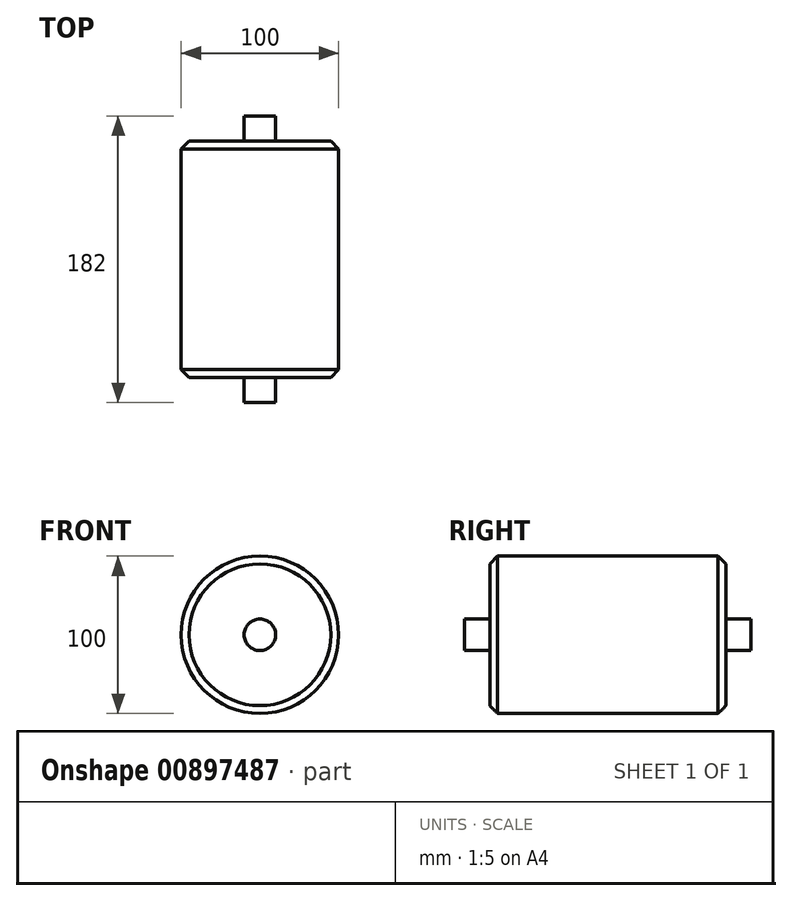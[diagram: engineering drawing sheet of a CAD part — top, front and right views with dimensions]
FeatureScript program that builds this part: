
annotation { "Feature Type Name" : "Feature", "Feature Type Description" : "" }
export const myFeature = defineFeature(function(context is Context, id is Id, definition is map)
    precondition{}
    {
        {
            var Q0;
            Q0=qCreatedBy(makeId("Front.planeOp"),FACE);
            var sketch = newSketch(context, id + "F0", { "sketchPlane" : qUnion([Q0])});
            skCircle(sketch, "E0", {"center": v(0, 0) * mm, "radius": 50 * mm});
            skSolve(sketch);
        }
        {
            var Q0;
            Q0 = qSketchRegion(id + "F0", true);
            extrude(context, id + "F1", {"entities" : qUnion([Q0]), "depth" : 75 * mm, "offsetDistance" : 25.4 * mm, "hasSecondDirection" : true, "secondDirectionOppositeDirection" : true, "secondDirectionDepth" : 75 * mm});
        }
        {
            var Q0;
            Q0=makeQuery(id+"F1.opExtrude","CAP_FACE",FACE,{"disambiguationData":[OSD([sQuery(id+"F0.wireOp",EDGE,"E0")])],"isStart":true});
            var sketch = newSketch(context, id + "F2", { "sketchPlane" : qUnion([Q0])});
            skCircle(sketch, "E1", {"center": v(0, 0) * mm, "radius": 10 * mm});
            skSolve(sketch);
        }
        {
            var Q0;
            Q0 = qSketchRegion(id + "F2", true);
            extrude(context, id + "F3", {"entities" : qUnion([Q0]), "operationType" : NewBodyOperationType.ADD, "depth" : 16 * mm, "offsetDistance" : 25.4 * mm});
        }
        {
            var Q0;
            Q0=makeQuery(id+"F1.opExtrude","CAP_FACE",FACE,{"disambiguationData":[OSD([sQuery(id+"F0.wireOp",EDGE,"E0")])],"isStart":false});
            var sketch = newSketch(context, id + "F4", { "sketchPlane" : qUnion([Q0])});
            skCircle(sketch, "E2", {"center": v(0, 0) * mm, "radius": 10 * mm});
            skSolve(sketch);
        }
        {
            var Q0;
            Q0 = qSketchRegion(id + "F4", true);
            extrude(context, id + "F5", {"entities" : qUnion([Q0]), "operationType" : NewBodyOperationType.ADD, "depth" : 16 * mm, "offsetDistance" : 25.4 * mm});
        }
        {
            var Q0;
            Q0=makeQuery(id+"F1.opExtrude","CAP_EDGE",EDGE,{"disambiguationData":[OSD([sQuery(id+"F0.wireOp",EDGE,"E0")])],"isStart":false});
            chamfer(context, id + "F6", {"entities" : qUnion([Q0]), "width" : 5 * mm, "tangentPropagation" : true});
        }
        {
            var Q0;
            Q0=makeQuery(id+"F1.opExtrude","CAP_EDGE",EDGE,{"disambiguationData":[OSD([sQuery(id+"F0.wireOp",EDGE,"E0")])],"isStart":true});
            chamfer(context, id + "F7", {"entities" : qUnion([Q0]), "width" : 5 * mm, "tangentPropagation" : true});
        }
    });
